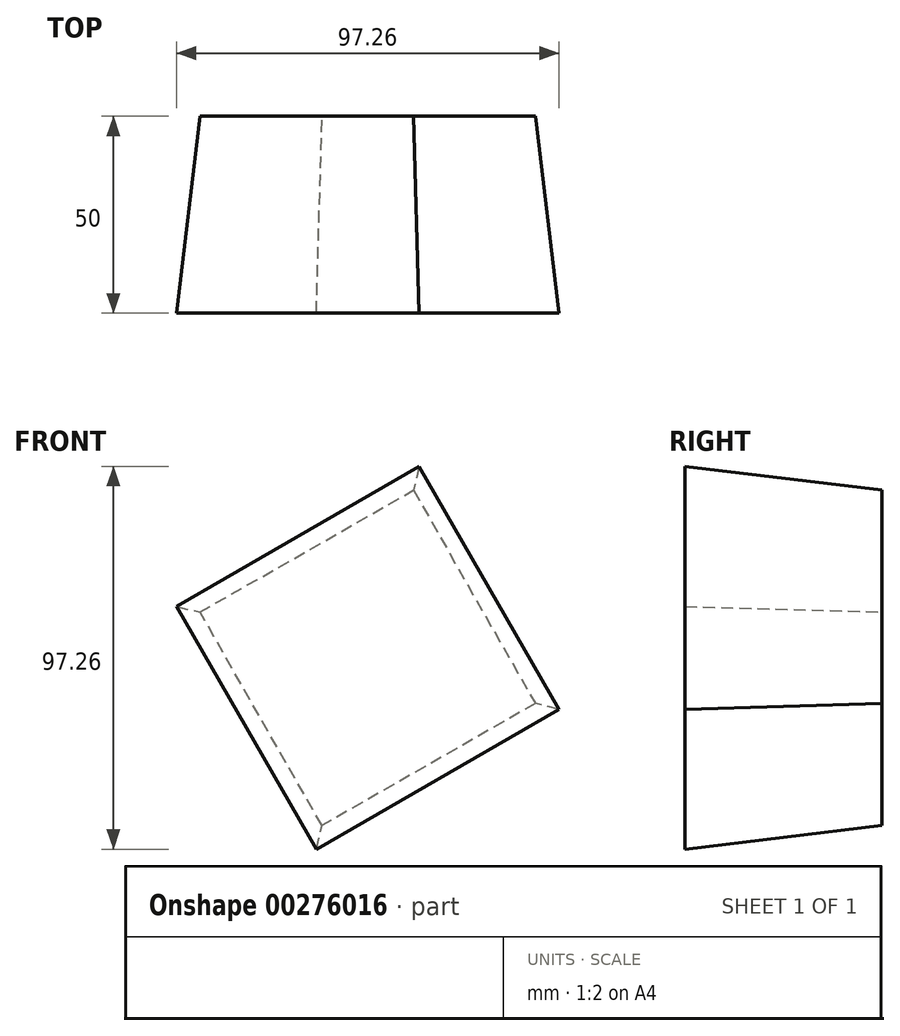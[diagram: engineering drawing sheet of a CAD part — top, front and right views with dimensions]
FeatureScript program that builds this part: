
annotation { "Feature Type Name" : "Feature", "Feature Type Description" : "" }
export const myFeature = defineFeature(function(context is Context, id is Id, definition is map)
    precondition{}
    {
        {
            var Q0;
            Q0=qCreatedBy(makeId("Front.planeOp"),FACE);
            var sketch = newSketch(context, id + "F0", { "sketchPlane" : qUnion([Q0])});
            skCircle(sketch, "E0.cCircle", {"center": v(0, 0) * mm, "radius": 31.22 * mm, "construction": true});
            skLineSegment(sketch, "E0.0", {"start": v(-42.6, 11.62) * mm, "end": v(11.62, 42.6) * mm});
            skLineSegment(sketch, "E0.1", {"start": v(11.62, 42.6) * mm, "end": v(42.6, -11.62) * mm});
            skLineSegment(sketch, "E0.2", {"start": v(42.6, -11.62) * mm, "end": v(-11.62, -42.6) * mm});
            skLineSegment(sketch, "E0.3", {"start": v(-11.62, -42.6) * mm, "end": v(-42.6, 11.62) * mm});
            skPoint(sketch, "E0.0.midPoint", {"position": v(-15.5, 27.11) * mm});
            skSolve(sketch);
        }
        {
            var Q0;
            Q0=qCreatedBy(makeId("Front.planeOp"),FACE);
            cPlane(context, id + "F1", {"entities" : qUnion([Q0]), "cplaneType" : CPlaneType.OFFSET, "offset" : 50 * mm, "width" : 150 * mm, "height" : 150 * mm});
        }
        {
            var Q0;
            Q0=qCreatedBy(id+"F1.planeOp",FACE);
            var sketch = newSketch(context, id + "F2", { "sketchPlane" : qUnion([Q0])});
            skCircle(sketch, "E1.cCircle", {"center": v(0, 0) * mm, "radius": 35.6 * mm, "construction": true});
            skLineSegment(sketch, "E1.0", {"start": v(-48.63, 13.05) * mm, "end": v(13.05, 48.63) * mm});
            skLineSegment(sketch, "E1.1", {"start": v(13.05, 48.63) * mm, "end": v(48.63, -13.05) * mm});
            skLineSegment(sketch, "E1.2", {"start": v(48.63, -13.05) * mm, "end": v(-13.05, -48.63) * mm});
            skLineSegment(sketch, "E1.3", {"start": v(-13.05, -48.63) * mm, "end": v(-48.63, 13.05) * mm});
            skPoint(sketch, "E1.0.midPoint", {"position": v(-17.79, 30.84) * mm});
            skSolve(sketch);
        }
        {
            var Q0;
            Q0=makeQuery(id+"F2.imprint","IMPRINT",FACE,{"disambiguationData":[TD([[makeQuery(id+"F2.imprint","IMPRINT",EDGE,{"derivedFrom":sQuery(id+"F2.wireOp",EDGE,"E1.0")}),-1.0]])]});
            var Q1;
            Q1=makeQuery(id+"F0.imprint","IMPRINT",FACE,{"disambiguationData":[TD([[makeQuery(id+"F0.imprint","IMPRINT",EDGE,{"derivedFrom":sQuery(id+"F0.wireOp",EDGE,"E0.0")}),-1.0]])]});
            loft(context, id + "F3", {"sheetProfilesArray" : [{ "sheetProfileEntities" : qUnion([Q0]) }, { "sheetProfileEntities" : qUnion([Q1]) }]});
        }
    });
